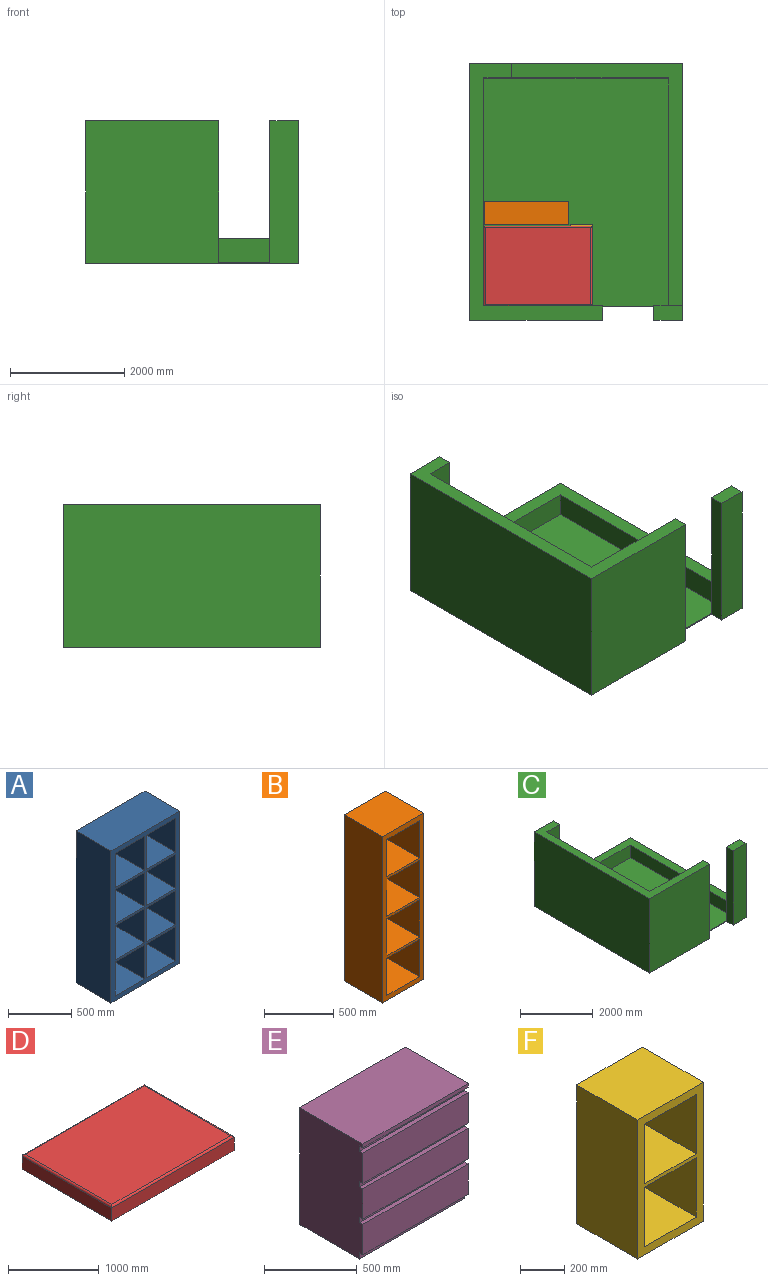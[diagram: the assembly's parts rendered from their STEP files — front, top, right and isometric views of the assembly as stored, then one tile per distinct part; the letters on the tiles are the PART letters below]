
ASSEMBLY  parts=6 mates=10
PART A: 38 faces, bbox 770x390x1470 mm
  f0: plane 1470x390mm, normal (-1,0,0), area 573300mm2, adj f1,f35,f36,f37
  f1: plane 770x390mm, normal (0,0,-1), area 300300mm2, adj f0,f2,f36,f37
  f2: plane 1470x390mm, normal (1,0,0), area 573300mm2, adj f1,f35,f36,f37
  f3: plane 390x330mm, normal (1,0,0), area 128700mm2, adj f4,f27,f36,f37
  f4: plane 390x330mm, normal (0,0,-1), area 128700mm2, adj f3,f5,f36,f37
  f5: plane 390x330mm, normal (-1,0,0), area 128700mm2, adj f4,f27,f36,f37
  f6: plane 390x330mm, normal (1,0,0), area 128700mm2, adj f7,f28,f36,f37
  f7: plane 390x330mm, normal (0,0,-1), area 128700mm2, adj f6,f8,f36,f37
  f8: plane 390x330mm, normal (-1,0,0), area 128700mm2, adj f7,f28,f36,f37
  f9: plane 390x330mm, normal (1,0,0), area 128700mm2, adj f10,f29,f36,f37
  f10: plane 390x330mm, normal (0,0,-1), area 128700mm2, adj f9,f11,f36,f37
  f11: plane 390x330mm, normal (-1,0,0), area 128700mm2, adj f10,f29,f36,f37
  f12: plane 390x330mm, normal (0,0,1), area 128700mm2, adj f13,f30,f36,f37
  f13: plane 390x330mm, normal (1,0,0), area 128700mm2, adj f12,f14,f36,f37
  f14: plane 390x330mm, normal (0,0,-1), area 128700mm2, adj f13,f30,f36,f37
  f15: plane 390x330mm, normal (0,0,-1), area 128700mm2, adj f16,f31,f36,f37
  f16: plane 390x330mm, normal (-1,0,0), area 128700mm2, adj f15,f17,f36,f37
  f17: plane 390x330mm, normal (0,0,1), area 128700mm2, adj f16,f31,f36,f37
  f18: plane 390x330mm, normal (0,0,1), area 128700mm2, adj f19,f32,f36,f37
  f19: plane 390x330mm, normal (1,0,0), area 128700mm2, adj f18,f20,f36,f37
  f20: plane 390x330mm, normal (0,0,-1), area 128700mm2, adj f19,f32,f36,f37
  f21: plane 390x330mm, normal (0,0,-1), area 128700mm2, adj f22,f33,f36,f37
  f22: plane 390x330mm, normal (-1,0,0), area 128700mm2, adj f21,f23,f36,f37
  f23: plane 390x330mm, normal (0,0,1), area 128700mm2, adj f22,f33,f36,f37
  f24: plane 390x330mm, normal (0,0,1), area 128700mm2, adj f25,f34,f36,f37
  f25: plane 390x330mm, normal (1,0,0), area 128700mm2, adj f24,f26,f36,f37
  f26: plane 390x330mm, normal (0,0,-1), area 128700mm2, adj f25,f34,f36,f37
  f27: plane 390x330mm, normal (0,0,1), area 128700mm2, adj f3,f5,f36,f37
  f28: plane 390x330mm, normal (0,0,1), area 128700mm2, adj f6,f8,f36,f37
  f29: plane 390x330mm, normal (0,0,1), area 128700mm2, adj f9,f11,f36,f37
  f30: plane 390x330mm, normal (-1,0,0), area 128700mm2, adj f12,f14,f36,f37
  f31: plane 390x330mm, normal (1,0,0), area 128700mm2, adj f15,f17,f36,f37
  f32: plane 390x330mm, normal (-1,0,0), area 128700mm2, adj f18,f20,f36,f37
  f33: plane 390x330mm, normal (1,0,0), area 128700mm2, adj f21,f23,f36,f37
  f34: plane 390x330mm, normal (-1,0,0), area 128700mm2, adj f24,f26,f36,f37
  f35: plane 770x390mm, normal (0,0,1), area 300300mm2, adj f0,f2,f36,f37
  f36: plane 1470x770mm, normal (0,-1,0), area 260700mm2, adj f0,f1,f2,f3,f4,f5,f6,f7
  f37: plane 1470x770mm, normal (0,1,0), area 260700mm2, adj f0,f1,f2,f3,f4,f5,f6,f7
PART B: 22 faces, bbox 420x390x1470 mm
  f0: plane 390x330mm, normal (1,0,0), area 128700mm2, adj f1,f19,f20,f21
  f1: plane 390x330mm, normal (0,0,-1), area 128700mm2, adj f0,f2,f20,f21
  f2: plane 390x330mm, normal (-1,0,0), area 128700mm2, adj f1,f19,f20,f21
  f3: plane 390x330mm, normal (1,0,0), area 128700mm2, adj f4,f15,f20,f21
  f4: plane 390x330mm, normal (0,0,-1), area 128700mm2, adj f3,f5,f20,f21
  f5: plane 390x330mm, normal (-1,0,0), area 128700mm2, adj f4,f15,f20,f21
  f6: plane 390x330mm, normal (0,0,-1), area 128700mm2, adj f7,f16,f20,f21
  f7: plane 390x330mm, normal (-1,0,0), area 128700mm2, adj f6,f8,f20,f21
  f8: plane 390x330mm, normal (0,0,1), area 128700mm2, adj f7,f16,f20,f21
  f9: plane 390x330mm, normal (0,0,-1), area 128700mm2, adj f10,f17,f20,f21
  f10: plane 390x330mm, normal (-1,0,0), area 128700mm2, adj f9,f11,f20,f21
  f11: plane 390x330mm, normal (0,0,1), area 128700mm2, adj f10,f17,f20,f21
  f12: plane 1470x390mm, normal (1,0,0), area 573300mm2, adj f13,f18,f20,f21
  f13: plane 420x390mm, normal (0,0,1), area 163800mm2, adj f12,f14,f20,f21
  f14: plane 1470x390mm, normal (-1,0,0), area 573300mm2, adj f13,f18,f20,f21
  f15: plane 390x330mm, normal (0,0,1), area 128700mm2, adj f3,f5,f20,f21
  f16: plane 390x330mm, normal (1,0,0), area 128700mm2, adj f6,f8,f20,f21
  f17: plane 390x330mm, normal (1,0,0), area 128700mm2, adj f9,f11,f20,f21
  f18: plane 420x390mm, normal (0,0,-1), area 163800mm2, adj f12,f14,f20,f21
  f19: plane 390x330mm, normal (0,0,1), area 128700mm2, adj f0,f2,f20,f21
  f20: plane 1470x420mm, normal (0,-1,0), area 181800mm2, adj f0,f1,f2,f3,f4,f5,f6,f7
  f21: plane 1470x420mm, normal (0,1,0), area 181800mm2, adj f0,f1,f2,f3,f4,f5,f6,f7
PART C: 20 faces, bbox 3730x4500x2500 mm
  f0: plane 4000x2480mm, normal (-1,0,0), area 1683877.7mm2, adj f1,f4,f13,f16,f17,f18
  f1: plane 3230x2480mm, normal (0,-1,0), area 2355538.4mm2, adj f0,f2,f8,f16,f17,f19
  f2: plane 4500x2330mm, normal (0,0,1), area 1767500mm2, adj f1,f3,f5,f6,f7,f8,f12,f19
  f3: plane 2480x2080mm, normal (0,1,0), area 5158400mm2, adj f2,f7,f8,f16
  f4: plane 2480x250mm, normal (0,1,0), area 620000mm2, adj f0,f9,f13,f16
  f5: plane 4500x2500mm, normal (-1,0,0), area 11250000mm2, adj f2,f6,f12,f14
  f6: plane 2500x2330mm, normal (0,-1,0), area 5825000mm2, adj f2,f5,f7,f14
  f7: plane 2500x250mm, normal (1,0,0), area 625000mm2, adj f2,f3,f6,f14,f15
  f8: plane 4000x2480mm, normal (1,0,0), area 9920000mm2, adj f1,f2,f3,f16
  f9: plane 2500x250mm, normal (-1,0,0), area 625000mm2, adj f4,f10,f13,f14,f15
  f10: plane 2500x500mm, normal (0,-1,0), area 1250000mm2, adj f9,f11,f13,f14
  f11: plane 4500x2500mm, normal (1,0,0), area 2497923.2mm2, adj f10,f12,f13,f14,f17,f18
  f12: plane 3730x2500mm, normal (0,1,0), area 3154183.9mm2, adj f2,f5,f11,f14,f17,f19
  f13: plane 500x259.28mm, normal (0,0,1), area 127319.7mm2, adj f0,f4,f9,f10,f11,f18
  f14: plane 4500x3730mm, normal (0,0,-1), area 16560000mm2, adj f5,f6,f7,f9,f10,f11,f12,f15
  f15: plane 900x20mm, normal (0,-1,0), area 18000mm2, adj f7,f9,f14,f16
  f16: plane 4000x3230mm, normal (0,0,1), area 12920000mm2, adj f0,f1,f3,f4,f8,f15
  f17: plane 4240.72x2990mm, normal (0,0,1), area 1745180.3mm2, adj f0,f1,f11,f12,f18,f19
  f18: plane 2063.82x250mm, normal (0,1,0), area 515954.5mm2, adj f0,f11,f13,f17
  f19: plane 2063.82x250mm, normal (1,0,0), area 515954.5mm2, adj f1,f2,f12,f17
PART D: 10 faces, bbox 1900x1400x200 mm
  f0: plane 1900x175mm, normal (0,1,0), area 332500mm2, adj f1,f3,f5,f6
  f1: plane 1400x175mm, normal (-1,0,0), area 245000mm2, adj f0,f2,f5,f7
  f2: plane 1900x175mm, normal (0,-1,0), area 332500mm2, adj f1,f3,f5,f9
  f3: plane 1400x175mm, normal (1,0,0), area 245000mm2, adj f0,f2,f5,f8
  f4: plane 1850x1350mm, normal (0,0,1), area 2497500mm2, adj f6,f7,f8,f9
  f5: plane 1900x1400mm, normal (0,0,-1), area 2660000mm2, adj f0,f1,f2,f3
  f6: cylinder r=25mm len=1900mm, axis (1,0,0), area 73899.3mm2, adj f0,f4,f7,f8
  f7: cylinder r=25mm len=1400mm, axis (0,1,0), area 54264.4mm2, adj f1,f4,f6,f9
  f8: cylinder r=25mm len=1400mm, axis (0,-1,0), area 54264.4mm2, adj f3,f4,f6,f9
  f9: cylinder r=25mm len=1900mm, axis (-1,0,0), area 73899.3mm2, adj f2,f4,f7,f8
PART E: 20 faces, bbox 800x480x770 mm
  f0: plane 800x455mm, normal (0,0,-1), area 364000mm2, adj f5,f6,f8,f19
  f1: plane 800x25mm, normal (0,-1,0), area 20000mm2, adj f5,f6,f7,f15
  f2: plane 800x200mm, normal (0,-1,0), area 160000mm2, adj f5,f6,f12,f16
  f3: plane 800x200mm, normal (0,-1,0), area 160000mm2, adj f5,f6,f9,f13
  f4: plane 800x200mm, normal (0,-1,0), area 160000mm2, adj f5,f6,f10,f18
  f5: plane 770x480mm, normal (-1,0,0), area 365975mm2, adj f0,f1,f2,f3,f4,f7,f8,f9
  f6: plane 770x480mm, normal (1,0,0), area 365975mm2, adj f0,f1,f2,f3,f4,f7,f8,f9
  f7: plane 800x480mm, normal (0,0,1), area 384000mm2, adj f1,f5,f6,f8
  f8: plane 800x770mm, normal (0,1,0), area 616000mm2, adj f0,f5,f6,f7
  f9: plane 800x25mm, normal (0,0,-1), area 20000mm2, adj f3,f5,f6,f11
  f10: plane 800x25mm, normal (0,0,1), area 20000mm2, adj f4,f5,f6,f11
  f11: plane 800x35mm, normal (0,-1,0), area 28000mm2, adj f5,f6,f9,f10
  f12: plane 800x25mm, normal (0,0,-1), area 20000mm2, adj f2,f5,f6,f14
  f13: plane 800x25mm, normal (0,0,1), area 20000mm2, adj f3,f5,f6,f14
  f14: plane 800x35mm, normal (0,-1,0), area 28000mm2, adj f5,f6,f12,f13
  f15: plane 800x25mm, normal (0,0,-1), area 20000mm2, adj f1,f5,f6,f17
  f16: plane 800x25mm, normal (0,0,1), area 20000mm2, adj f2,f5,f6,f17
  f17: plane 800x35mm, normal (0,-1,0), area 28000mm2, adj f5,f6,f15,f16
  f18: plane 800x25mm, normal (0,0,-1), area 20000mm2, adj f4,f5,f6,f19
  f19: plane 800x40mm, normal (0,-1,0), area 32000mm2, adj f0,f5,f6,f18
PART F: 14 faces, bbox 420x390x770 mm
  f0: plane 770x390mm, normal (-1,0,0), area 300300mm2, adj f1,f11,f12,f13
  f1: plane 420x390mm, normal (0,0,-1), area 163800mm2, adj f0,f2,f12,f13
  f2: plane 770x390mm, normal (1,0,0), area 300300mm2, adj f1,f11,f12,f13
  f3: plane 390x330mm, normal (1,0,0), area 128700mm2, adj f4,f9,f12,f13
  f4: plane 390x330mm, normal (0,0,-1), area 128700mm2, adj f3,f5,f12,f13
  f5: plane 390x330mm, normal (-1,0,0), area 128700mm2, adj f4,f9,f12,f13
  f6: plane 390x330mm, normal (0,0,-1), area 128700mm2, adj f7,f10,f12,f13
  f7: plane 390x330mm, normal (-1,0,0), area 128700mm2, adj f6,f8,f12,f13
  f8: plane 390x330mm, normal (0,0,1), area 128700mm2, adj f7,f10,f12,f13
  f9: plane 390x330mm, normal (0,0,1), area 128700mm2, adj f3,f5,f12,f13
  f10: plane 390x330mm, normal (1,0,0), area 128700mm2, adj f6,f8,f12,f13
  f11: plane 420x390mm, normal (0,0,1), area 163800mm2, adj f0,f2,f12,f13
  f12: plane 770x420mm, normal (0,-1,0), area 105600mm2, adj f0,f1,f2,f3,f4,f5,f6,f7
  f13: plane 770x420mm, normal (0,1,0), area 105600mm2, adj f0,f1,f2,f3,f4,f5,f6,f7
PLACE A rot(axis=(0.71,0,0.71),180deg) t=(-1520.38,-1041.52,-1041.18)mm
PLACE B rot(axis=(0,1,0),90deg) t=(-1508.72,-224.48,-925.83)mm
PLACE C t=(17375.39,-1646.3,-1213.5)mm fixed
PLACE D rot(axis=(0,0,1),180deg) t=(-811.18,-1099.23,-423.55)mm
PLACE E rot(axis=(0,0,1),90deg) t=(-326.38,-1952.44,-1140.58)mm
PLACE F rot(axis=(0,0,-1),90deg) t=(162.16,-774.54,-967.51)mm
MATE planar E.f5 <-> C.f3  axis (0,-1,0) through (-88.63,-2051.52,-808.28)mm
MATE planar B.f12 <-> C.f16  axis (0,0,-1) through (-999.72,-419.48,-1193.5)mm
MATE planar D.f2 <-> A.f36  axis (0,1,0) through (-796.38,-651.52,-336.05)mm
MATE planar A.f0 <-> C.f16  axis (0,0,-1) through (-1011.38,-846.52,-1193.5)mm
MATE planar D.f0 <-> C.f3  axis (0,-1,0) through (-796.38,-2051.52,-336.05)mm
MATE planar D.f1 <-> E.f2  axis (1,0,0) through (153.62,-1351.52,-336.05)mm
MATE planar E.f0 <-> C.f16  axis (0,0,-1) through (-98.88,-1651.52,-1193.5)mm
MATE planar A.f1 <-> C.f8  axis (-1,0,0) through (-1746.38,-846.52,-808.5)mm
MATE planar D.f3 <-> C.f8  axis (-1,0,0) through (-1746.38,-1351.52,-336.05)mm
MATE planar F.f1 <-> C.f16  axis (0,0,-1) through (-32.84,-832.22,-1193.5)mm
